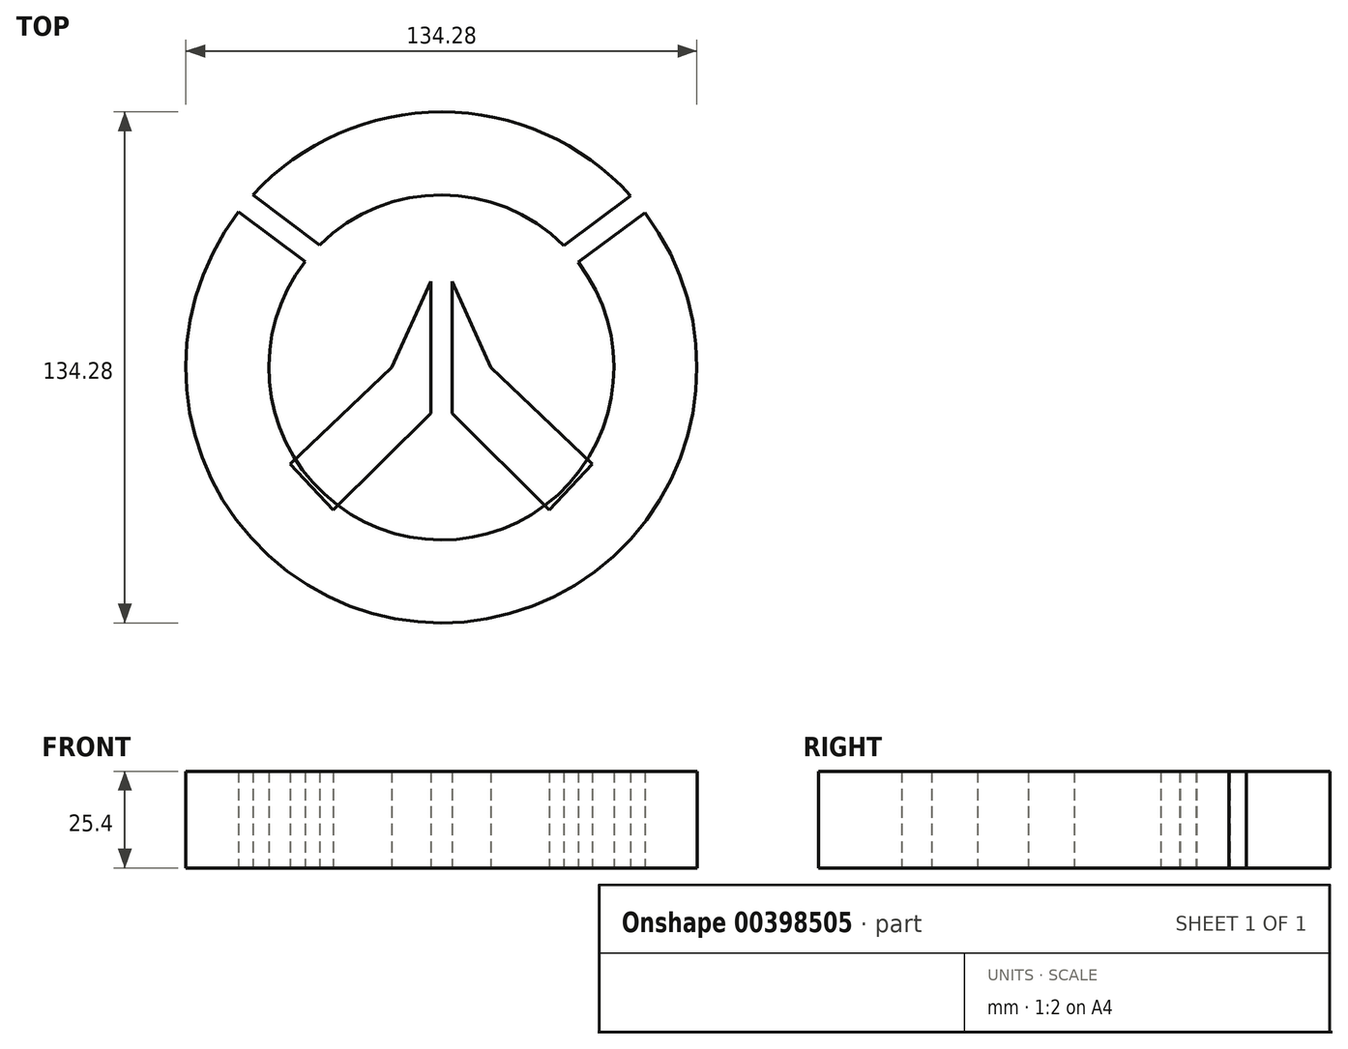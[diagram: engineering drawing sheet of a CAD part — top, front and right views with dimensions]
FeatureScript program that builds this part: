
annotation { "Feature Type Name" : "Feature", "Feature Type Description" : "" }
export const myFeature = defineFeature(function(context is Context, id is Id, definition is map)
    precondition{}
    {
        {
            var Q0;
            Q0=qCreatedBy(makeId("Top.planeOp"),FACE);
            var sketch = newSketch(context, id + "F0", { "sketchPlane" : qUnion([Q0])});
            skCircle(sketch, "E0", {"center": v(0, 0) * mm, "radius": 67.14 * mm});
            skSolve(sketch);
        }
        {
            var Q0;
            Q0 = qSketchRegion(id + "F0", true);
            extrude(context, id + "F1", {"entities" : qUnion([Q0]), "depth" : 25.4 * mm});
        }
        {
            var Q0;
            Q0=qCreatedBy(makeId("Top.planeOp"),FACE);
            var sketch = newSketch(context, id + "F2", { "sketchPlane" : qUnion([Q0])});
            skCircle(sketch, "E1", {"center": v(0, 0) * mm, "radius": 45.34 * mm});
            skSolve(sketch);
        }
        {
            var Q0;
            Q0 = qSketchRegion(id + "F2", true);
            extrude(context, id + "F3", {"entities" : qUnion([Q0]), "operationType" : NewBodyOperationType.REMOVE, "depth" : 25.4 * mm});
        }
        {
            var Q0;
            Q0=qCreatedBy(makeId("Top.planeOp"),FACE);
            var sketch = newSketch(context, id + "F4", { "sketchPlane" : qUnion([Q0])});
            skLineSegment(sketch, "E2", {"start": v(-35.66, 27.7) * mm, "end": v(37.98, 27.7) * mm, "construction": true});
            skLineSegment(sketch, "E3", {"start": v(-35.66, 27.7) * mm, "end": v(-57.1, 43.67) * mm});
            skLineSegment(sketch, "E4", {"start": v(-57.1, 43.67) * mm, "end": v(-53.63, 48.33) * mm});
            skLineSegment(sketch, "E5", {"start": v(-53.63, 48.33) * mm, "end": v(-31.1, 31.55) * mm});
            skLineSegment(sketch, "E6", {"start": v(-31.1, 31.55) * mm, "end": v(-35.66, 27.7) * mm});
            skLineSegment(sketch, "E7.MirrorCS", {"start": v(57.15, 43.44) * mm, "end": v(53.68, 48.1) * mm});
            skLineSegment(sketch, "E8.MirrorCS", {"start": v(53.68, 48.1) * mm, "end": v(31.15, 31.31) * mm});
            skLineSegment(sketch, "E9.MirrorCS", {"start": v(35.71, 27.47) * mm, "end": v(57.15, 43.44) * mm});
            skLineSegment(sketch, "E10.MirrorCS", {"start": v(31.15, 31.31) * mm, "end": v(35.71, 27.47) * mm});
            skSolve(sketch);
        }
        {
            var Q0;
            Q0 = qSketchRegion(id + "F4", true);
            extrude(context, id + "F5", {"entities" : qUnion([Q0]), "operationType" : NewBodyOperationType.REMOVE, "depth" : 25.4 * mm});
        }
        {
            var Q0;
            Q0 = qSketchRegion(id + "F4", true);
            extrude(context, id + "F6", {"entities" : qUnion([Q0]), "operationType" : NewBodyOperationType.REMOVE, "depth" : 25.4 * mm});
        }
        {
            var Q0;
            Q0=qCreatedBy(makeId("Top.planeOp"),FACE);
            var sketch = newSketch(context, id + "F7", { "sketchPlane" : qUnion([Q0])});
            skLineSegment(sketch, "E11", {"start": v(-2.8, 22.66) * mm, "end": v(-13.02, 0) * mm});
            skLineSegment(sketch, "E12", {"start": v(-39.7, -25.44) * mm, "end": v(-28.38, -37.45) * mm});
            skLineSegment(sketch, "E13", {"start": v(-28.38, -37.45) * mm, "end": v(-2.8, -12.1) * mm});
            skLineSegment(sketch, "E14", {"start": v(-13.02, 0) * mm, "end": v(-39.7, -25.44) * mm});
            skLineSegment(sketch, "E15", {"start": v(0, 35.82) * mm, "end": v(0, -29.54) * mm, "construction": true});
            skLineSegment(sketch, "E16", {"start": v(-2.8, 22.66) * mm, "end": v(-2.8, -12.1) * mm});
            skLineSegment(sketch, "E17.MirrorCS", {"start": v(2.8, 22.66) * mm, "end": v(2.8, -12.1) * mm});
            skLineSegment(sketch, "E18.MirrorCS", {"start": v(2.8, 22.66) * mm, "end": v(13.02, 0) * mm});
            skLineSegment(sketch, "E19.MirrorCS", {"start": v(28.38, -37.45) * mm, "end": v(2.8, -12.1) * mm});
            skLineSegment(sketch, "E20.MirrorCS", {"start": v(13.02, 0) * mm, "end": v(39.7, -25.44) * mm});
            skLineSegment(sketch, "E21.MirrorCS", {"start": v(39.7, -25.44) * mm, "end": v(28.38, -37.45) * mm});
            skSolve(sketch);
        }
        {
            var Q0;
            Q0 = qSketchRegion(id + "F7", true);
            extrude(context, id + "F8", {"entities" : qUnion([Q0]), "depth" : 25.4 * mm});
        }
    });
